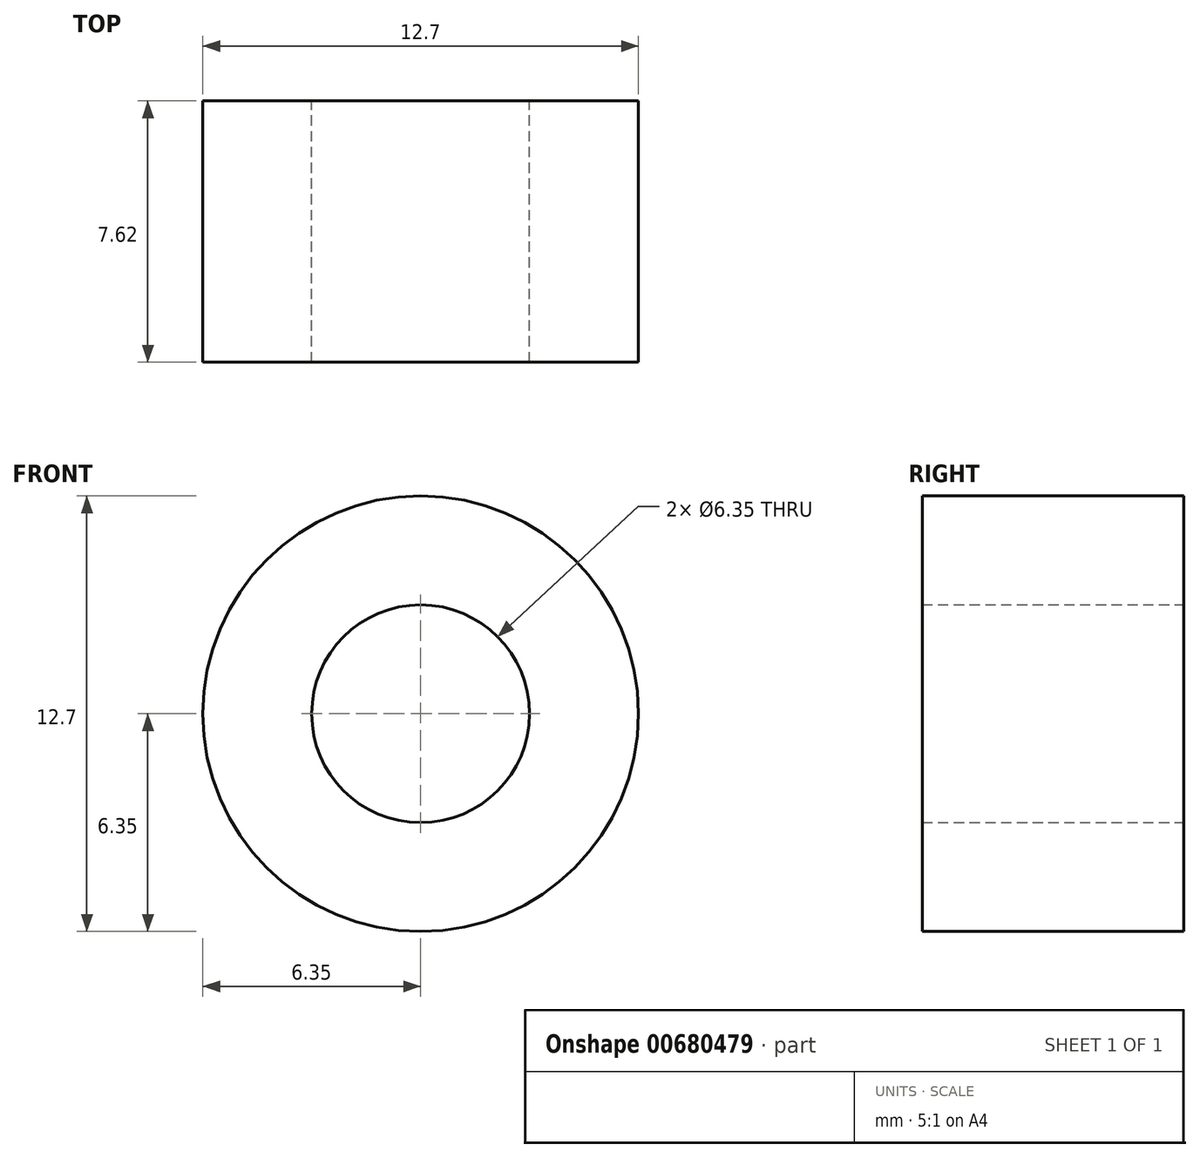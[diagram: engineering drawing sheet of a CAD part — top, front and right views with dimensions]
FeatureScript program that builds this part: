
annotation { "Feature Type Name" : "Feature", "Feature Type Description" : "" }
export const myFeature = defineFeature(function(context is Context, id is Id, definition is map)
    precondition{}
    {
        {
            var Q0;
            Q0=qCreatedBy(makeId("Front.planeOp"),FACE);
            var sketch = newSketch(context, id + "F0", { "sketchPlane" : qUnion([Q0])});
            skCircle(sketch, "E0", {"center": v(0, 0) * mm, "radius": 6.35 * mm});
            skCircle(sketch, "E1", {"center": v(0, 0) * mm, "radius": 3.18 * mm});
            skSolve(sketch);
        }
        {
            var Q0;
            Q0=makeQuery(id+"F0.imprint","IMPRINT",FACE,{"disambiguationData":[TD([[makeQuery(id+"F0.imprint","IMPRINT",EDGE,{"derivedFrom":sQuery(id+"F0.wireOp",EDGE,"E0")}),1.0]])]});
            extrude(context, id + "F1", {"entities" : qUnion([Q0]), "depth" : 7.62 * mm, "offsetDistance" : 25.4 * mm});
        }
    });
